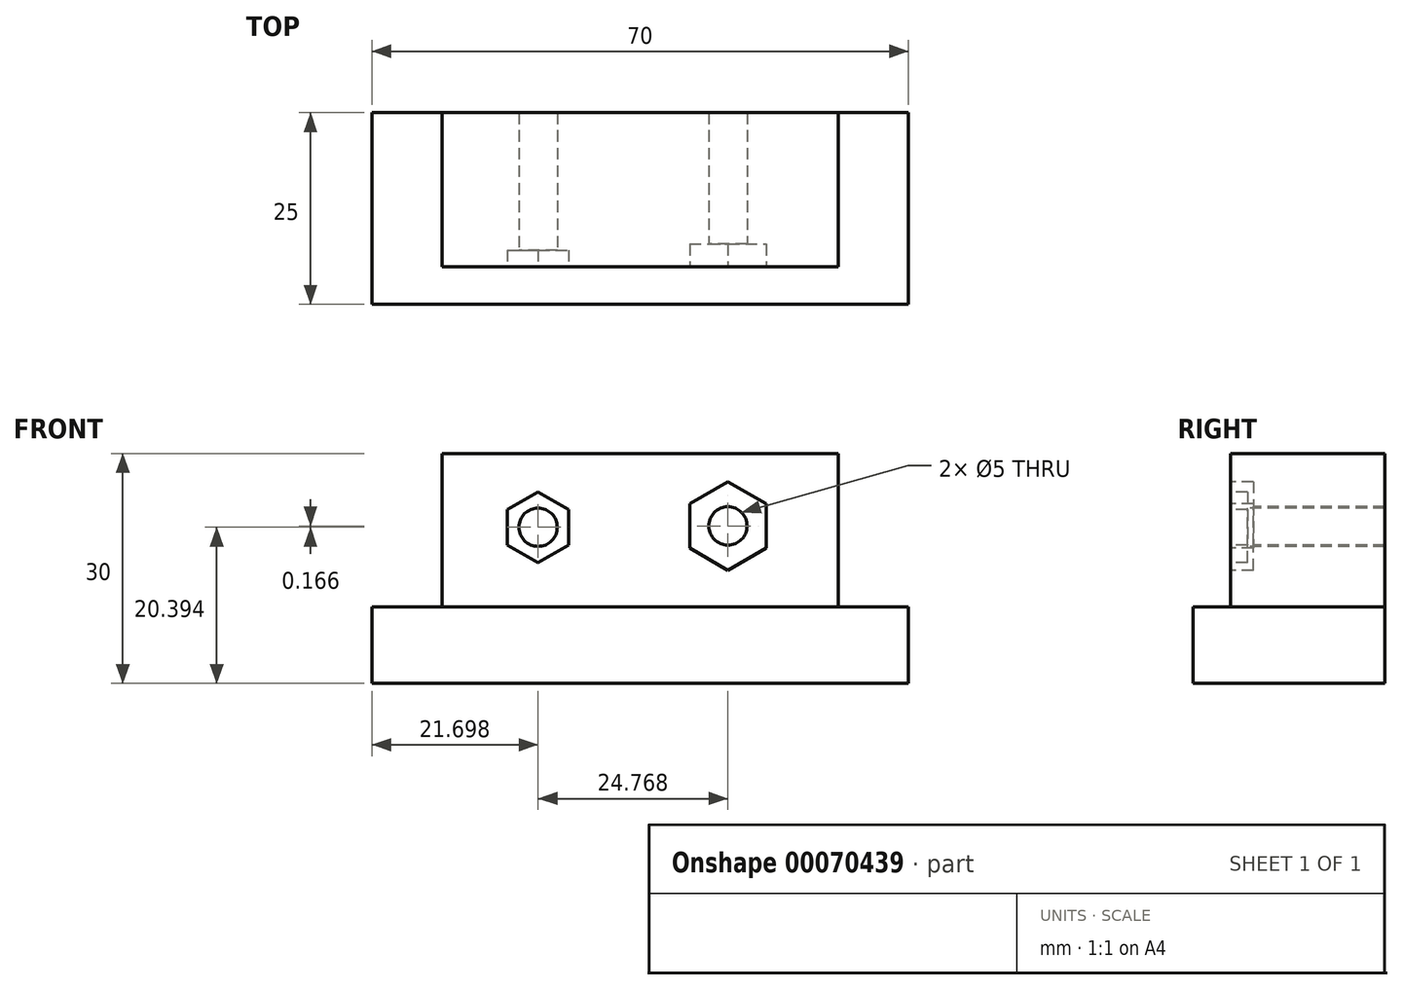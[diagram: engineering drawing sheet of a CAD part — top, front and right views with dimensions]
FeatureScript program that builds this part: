
annotation { "Feature Type Name" : "Feature", "Feature Type Description" : "" }
export const myFeature = defineFeature(function(context is Context, id is Id, definition is map)
    precondition{}
    {
        {
            var Q0;
            Q0=qCreatedBy(makeId("Top.planeOp"),FACE);
            var sketch = newSketch(context, id + "F0", { "sketchPlane" : qUnion([Q0])});
            skLineSegment(sketch, "E0.rect.bottom", {"start": v(35, 25) * mm, "end": v(-35, 25) * mm});
            skLineSegment(sketch, "E0.rect.top", {"start": v(35, -25) * mm, "end": v(-35, -25) * mm});
            skLineSegment(sketch, "E0.rect.left", {"start": v(35, 25) * mm, "end": v(35, -25) * mm});
            skLineSegment(sketch, "E0.rect.right", {"start": v(-35, 25) * mm, "end": v(-35, -25) * mm});
            skPoint(sketch, "E0.rect.middle", {"position": v(0, 0) * mm});
            skSolve(sketch);
        }
        {
            var Q0;
            Q0=makeQuery(id+"F0.imprint","IMPRINT",FACE,{"disambiguationData":[TD([[makeQuery(id+"F0.imprint","IMPRINT",EDGE,{"derivedFrom":sQuery(id+"F0.wireOp",EDGE,"E0.rect.bottom")}),1.0]])]});
            extrude(context, id + "F1", {"entities" : qUnion([Q0]), "depth" : 10 * mm});
        }
        {
            var Q0;
            Q0=makeQuery(id+"F1.opExtrude","CAP_FACE",FACE,{"disambiguationData":[OSD([sQuery(id+"F0.wireOp",EDGE,"E0.rect.bottom"),sQuery(id+"F0.wireOp",EDGE,"E0.rect.top"),sQuery(id+"F0.wireOp",EDGE,"E0.rect.left"),sQuery(id+"F0.wireOp",EDGE,"E0.rect.right")])],"isStart":false});
            var sketch = newSketch(context, id + "F2", { "sketchPlane" : qUnion([Q0])});
            skLineSegment(sketch, "E1.rect.bottom", {"start": v(-25.85, 20.13) * mm, "end": v(25.85, 20.13) * mm});
            skLineSegment(sketch, "E1.rect.top", {"start": v(-25.85, -20.13) * mm, "end": v(25.85, -20.13) * mm});
            skLineSegment(sketch, "E1.rect.left", {"start": v(-25.85, 20.13) * mm, "end": v(-25.85, -20.13) * mm});
            skLineSegment(sketch, "E1.rect.right", {"start": v(25.85, 20.13) * mm, "end": v(25.85, -20.13) * mm});
            skPoint(sketch, "E1.rect.middle", {"position": v(0, 0) * mm});
            skSolve(sketch);
        }
        {
            var Q0;
            Q0 = qSketchRegion(id + "F2", true);
            extrude(context, id + "F3", {"entities" : qUnion([Q0]), "operationType" : NewBodyOperationType.ADD, "depth" : 20 * mm});
        }
        {
            var Q0;
            Q0=makeQuery(id+"F3.opExtrude","SWEPT_FACE",FACE,{"disambiguationData":[OSD([sQuery(id+"F2.wireOp",EDGE,"E1.rect.top")])]});
            var sketch = newSketch(context, id + "F4", { "sketchPlane" : qUnion([Q0])});
            skCircle(sketch, "E2.cCircle", {"center": v(-13.3, 20.4) * mm, "radius": 4 * mm, "construction": true});
            skLineSegment(sketch, "E2.0", {"start": v(-9.3, 22.7) * mm, "end": v(-9.3, 18.08) * mm});
            skLineSegment(sketch, "E2.1", {"start": v(-9.3, 18.08) * mm, "end": v(-13.3, 15.78) * mm});
            skLineSegment(sketch, "E2.2", {"start": v(-13.3, 15.78) * mm, "end": v(-17.3, 18.08) * mm});
            skLineSegment(sketch, "E2.3", {"start": v(-17.3, 18.08) * mm, "end": v(-17.3, 22.7) * mm});
            skLineSegment(sketch, "E2.4", {"start": v(-17.3, 22.7) * mm, "end": v(-13.3, 25.01) * mm});
            skLineSegment(sketch, "E2.5", {"start": v(-13.3, 25.01) * mm, "end": v(-9.3, 22.7) * mm});
            skPoint(sketch, "E2.0.midPoint", {"position": v(-9.3, 20.4) * mm});
            skSolve(sketch);
        }
        {
            var Q0;
            Q0 = qSketchRegion(id + "F4", true);
            extrude(context, id + "F5", {"entities" : qUnion([Q0]), "operationType" : NewBodyOperationType.REMOVE, "oppositeDirection" : true, "depth" : 2.2 * mm});
        }
        {
            var Q0;
            Q0=makeQuery(id+"F5.boolean.opBoolean","COPY",FACE,{"derivedFrom":makeQuery(id+"F5.opExtrude","CAP_FACE",FACE,{"disambiguationData":[OSD([sQuery(id+"F4.wireOp",EDGE,"E2.0"),sQuery(id+"F4.wireOp",EDGE,"E2.1"),sQuery(id+"F4.wireOp",EDGE,"E2.2"),sQuery(id+"F4.wireOp",EDGE,"E2.3"),sQuery(id+"F4.wireOp",EDGE,"E2.4"),sQuery(id+"F4.wireOp",EDGE,"E2.5")])],"isStart":false})});
            var sketch = newSketch(context, id + "F6", { "sketchPlane" : qUnion([Q0])});
            skLineSegment(sketch, "E3", {"start": v(-13.3, 25.01) * mm, "end": v(-13.3, 15.78) * mm, "construction": true});
            skLineSegment(sketch, "E4", {"start": v(-17.3, 22.7) * mm, "end": v(-9.3, 18.08) * mm, "construction": true});
            skCircle(sketch, "E5", {"center": v(-13.3, 20.4) * mm, "radius": 2.5 * mm});
            skSolve(sketch);
        }
        {
            var Q0;
            Q0 = qSketchRegion(id + "F6", true);
            var Q1;
            Q1=sQuery(id+"F6.wireOp",EDGE,"E5");
            extrude(context, id + "F7", {"entities" : qUnion([Q0]), "operationType" : NewBodyOperationType.REMOVE, "surfaceEntities" : qUnion([Q1]), "endBound" : BoundingType.THROUGH_ALL, "oppositeDirection" : true, "depth" : 25.4 * mm});
        }
        {
            var Q0;
            Q0=makeQuery(id+"F3.opExtrude","SWEPT_FACE",FACE,{"disambiguationData":[OSD([sQuery(id+"F2.wireOp",EDGE,"E1.rect.top")])]});
            var sketch = newSketch(context, id + "F8", { "sketchPlane" : qUnion([Q0])});
            skCircle(sketch, "E6.cCircle", {"center": v(11.47, 20.56) * mm, "radius": 5 * mm, "construction": true});
            skLineSegment(sketch, "E6.0", {"start": v(16.47, 23.45) * mm, "end": v(16.47, 17.67) * mm});
            skLineSegment(sketch, "E6.1", {"start": v(16.47, 17.67) * mm, "end": v(11.47, 14.79) * mm});
            skLineSegment(sketch, "E6.2", {"start": v(11.47, 14.79) * mm, "end": v(6.47, 17.67) * mm});
            skLineSegment(sketch, "E6.3", {"start": v(6.47, 17.67) * mm, "end": v(6.47, 23.45) * mm});
            skLineSegment(sketch, "E6.4", {"start": v(6.47, 23.45) * mm, "end": v(11.47, 26.33) * mm});
            skLineSegment(sketch, "E6.5", {"start": v(11.47, 26.33) * mm, "end": v(16.47, 23.45) * mm});
            skPoint(sketch, "E6.0.midPoint", {"position": v(16.47, 20.56) * mm});
            skSolve(sketch);
        }
        {
            var Q0;
            Q0 = qSketchRegion(id + "F8", true);
            extrude(context, id + "F9", {"entities" : qUnion([Q0]), "operationType" : NewBodyOperationType.REMOVE, "oppositeDirection" : true, "depth" : 3 * mm});
        }
        {
            var Q0;
            Q0=makeQuery(id+"F9.boolean.opBoolean","COPY",FACE,{"derivedFrom":makeQuery(id+"F9.opExtrude","CAP_FACE",FACE,{"disambiguationData":[OSD([sQuery(id+"F8.wireOp",EDGE,"E6.0"),sQuery(id+"F8.wireOp",EDGE,"E6.1"),sQuery(id+"F8.wireOp",EDGE,"E6.2"),sQuery(id+"F8.wireOp",EDGE,"E6.3"),sQuery(id+"F8.wireOp",EDGE,"E6.4"),sQuery(id+"F8.wireOp",EDGE,"E6.5")])],"isStart":false})});
            var sketch = newSketch(context, id + "F10", { "sketchPlane" : qUnion([Q0])});
            skLineSegment(sketch, "E7", {"start": v(6.47, 23.45) * mm, "end": v(16.47, 17.67) * mm, "construction": true});
            skLineSegment(sketch, "E8", {"start": v(11.47, 26.33) * mm, "end": v(11.47, 14.79) * mm, "construction": true});
            skCircle(sketch, "E9", {"center": v(11.47, 20.56) * mm, "radius": 2.5 * mm});
            skSolve(sketch);
        }
        {
            var Q0;
            Q0 = qSketchRegion(id + "F10", true);
            extrude(context, id + "F11", {"entities" : qUnion([Q0]), "operationType" : NewBodyOperationType.REMOVE, "endBound" : BoundingType.THROUGH_ALL, "oppositeDirection" : true, "depth" : 25.4 * mm});
        }
        {
            var Q0;
            Q0=qCreatedBy(makeId("Top.planeOp"),FACE);
            var sketch = newSketch(context, id + "F12", { "sketchPlane" : qUnion([Q0])});
            skLineSegment(sketch, "E10.rect.bottom", {"start": v(50.52, 0) * mm, "end": v(-50.52, 0) * mm});
            skLineSegment(sketch, "E10.rect.top", {"start": v(50.52, 53.5) * mm, "end": v(-50.52, 53.5) * mm});
            skLineSegment(sketch, "E10.rect.left", {"start": v(50.52, 0) * mm, "end": v(50.52, 53.5) * mm});
            skLineSegment(sketch, "E10.rect.right", {"start": v(-50.52, 0) * mm, "end": v(-50.52, 53.5) * mm});
            skPoint(sketch, "E10.rect.middle", {"position": v(0, 26.75) * mm});
            skSolve(sketch);
        }
        {
            var Q0;
            Q0=makeQuery(id+"F12.imprint","IMPRINT",FACE,{"disambiguationData":[TD([[makeQuery(id+"F12.imprint","IMPRINT",EDGE,{"derivedFrom":sQuery(id+"F12.wireOp",EDGE,"E10.rect.bottom")}),-1.0]])]});
            extrude(context, id + "F13", {"entities" : qUnion([Q0]), "operationType" : NewBodyOperationType.REMOVE, "endBound" : BoundingType.THROUGH_ALL, "depth" : 25.4 * mm});
        }
    });
